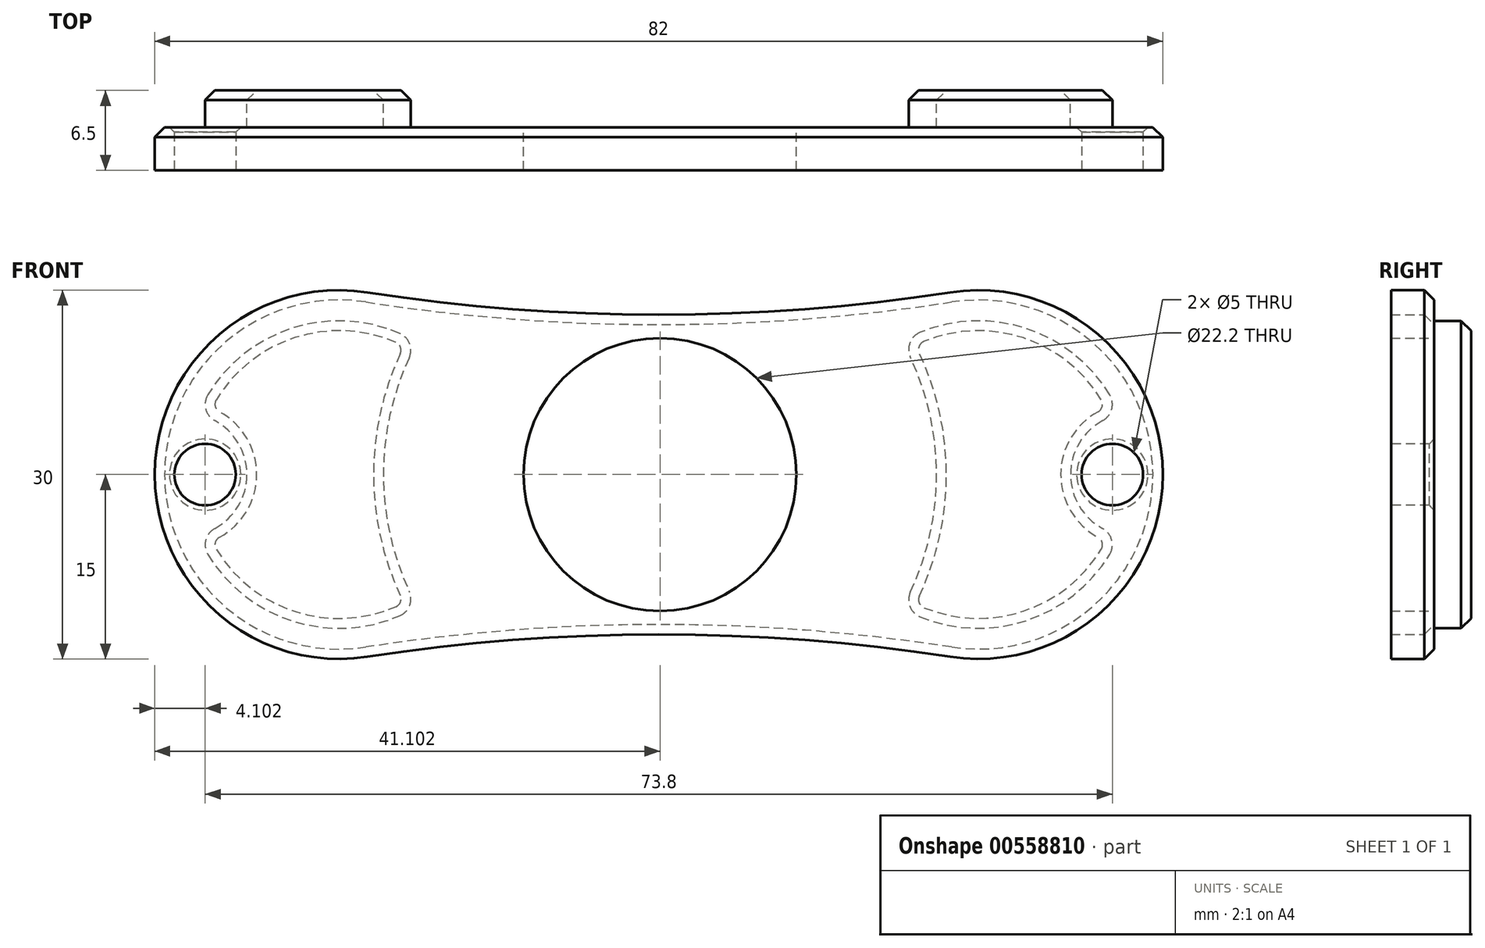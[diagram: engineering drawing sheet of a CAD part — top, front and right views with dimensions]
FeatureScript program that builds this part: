
annotation { "Feature Type Name" : "Feature", "Feature Type Description" : "" }
export const myFeature = defineFeature(function(context is Context, id is Id, definition is map)
    precondition{}
    {
        {
            var Q0;
            Q0=qCreatedBy(makeId("Front.planeOp"),FACE);
            var sketch = newSketch(context, id + "F0", { "sketchPlane" : qUnion([Q0])});
            skCircle(sketch, "E0", {"center": v(-1.84, 0) * mm, "radius": 11.1 * mm});
            skArc(sketch, "E1", {"start": v(-25.64, 14.82) * mm, "mid": v(-42.94, 0) * mm, "end": v(-25.64, -14.82) * mm});
            skArc(sketch, "E2", {"start": v(-25.64, 14.82) * mm, "mid": v(-1.94, 13) * mm, "end": v(21.77, 14.82) * mm});
            skArc(sketch, "E3", {"start": v(21.77, -14.82) * mm, "mid": v(-1.94, -13) * mm, "end": v(-25.64, -14.82) * mm});
            skArc(sketch, "E4.trimOffspring", {"start": v(21.77, -14.82) * mm, "mid": v(39.06, 0) * mm, "end": v(21.77, 14.82) * mm});
            skSolve(sketch);
        }
        {
            var Q0;
            Q0=makeQuery(id+"F0.imprint","IMPRINT",FACE,{"disambiguationData":[TD([[makeQuery(id+"F0.imprint","IMPRINT",EDGE,{"derivedFrom":sQuery(id+"F0.wireOp",EDGE,"E0")}),-1.0]])]});
            extrude(context, id + "F1", {"entities" : qUnion([Q0]), "depth" : 7 * mm, "offsetDistance" : 25 * mm});
        }
        {
            var Q0;
            Q0=makeQuery(id+"F1.opExtrude","CAP_EDGE",EDGE,{"disambiguationData":[OSD([sQuery(id+"F0.wireOp",EDGE,"E1")])],"isStart":false});
            var Q1;
            Q1=makeQuery(id+"F1.opExtrude","CAP_EDGE",EDGE,{"disambiguationData":[OSD([sQuery(id+"F0.wireOp",EDGE,"E3")])],"isStart":false});
            var Q2;
            Q2=makeQuery(id+"F1.opExtrude","CAP_EDGE",EDGE,{"disambiguationData":[OSD([sQuery(id+"F0.wireOp",EDGE,"E3")])],"isStart":true});
            chamfer(context, id + "F2", {"entities" : qUnion([Q0, Q1, Q2]), "width" : .8 * mm, "tangentPropagation" : true});
        }
        {
            var Q0;
            Q0=makeQuery(id+"F1.opExtrude","CAP_FACE",FACE,{"disambiguationData":[OSD([sQuery(id+"F0.wireOp",EDGE,"E0"),sQuery(id+"F0.wireOp",EDGE,"E1"),sQuery(id+"F0.wireOp",EDGE,"E2"),sQuery(id+"F0.wireOp",EDGE,"E3"),sQuery(id+"F0.wireOp",EDGE,"E4.trimOffspring")])],"isStart":false});
            var sketch = newSketch(context, id + "F3", { "sketchPlane" : qUnion([Q0])});
            skCircle(sketch, "E5", {"center": v(-27.94, 0) * mm, "radius": 12.5 * mm});
            skCircle(sketch, "E6", {"center": v(24.06, 0) * mm, "radius": 12.5 * mm});
            skSolve(sketch);
        }
        {
            var Q0;
            Q0=qSketchRegion(id+"F3",true);
            extrude(context, id + "F4", {"entities" : qUnion([Q0]), "operationType" : NewBodyOperationType.ADD, "depth" : 3 * mm, "offsetDistance" : 25 * mm});
        }
        {
            var Q0;
            Q0=makeQuery(id+"F1.opExtrude","CAP_FACE",FACE,{"disambiguationData":[OSD([sQuery(id+"F0.wireOp",EDGE,"E0"),sQuery(id+"F0.wireOp",EDGE,"E1"),sQuery(id+"F0.wireOp",EDGE,"E2"),sQuery(id+"F0.wireOp",EDGE,"E3"),sQuery(id+"F0.wireOp",EDGE,"E4.trimOffspring")])],"isStart":true});
            var sketch = newSketch(context, id + "F5", { "sketchPlane" : qUnion([Q0])});
            skCircle(sketch, "E7", {"center": v(-24.06, 0) * mm, "radius": 12.5 * mm});
            skCircle(sketch, "E8", {"center": v(27.94, 0) * mm, "radius": 12.5 * mm});
            skSolve(sketch);
        }
        {
            var Q0;
            Q0=qSketchRegion(id+"F5",true);
            extrude(context, id + "F6", {"entities" : qUnion([Q0]), "operationType" : NewBodyOperationType.ADD, "depth" : 3 * mm, "offsetDistance" : 25 * mm});
        }
        {
            var Q0;
            Q0=makeQuery(id+"F4.opExtrude","CAP_FACE",FACE,{"disambiguationData":[OSD([sQuery(id+"F3.wireOp",EDGE,"E6")])],"isStart":false});
            var sketch = newSketch(context, id + "F7", { "sketchPlane" : qUnion([Q0])});
            skSolve(sketch);
        }
        {
            var Q0;
            Q0=makeQuery(id+"F4.opExtrude","CAP_FACE",FACE,{"disambiguationData":[OSD([sQuery(id+"F3.wireOp",EDGE,"E5")])],"isStart":false});
            var sketch = newSketch(context, id + "F8", { "sketchPlane" : qUnion([Q0])});
            skCircle(sketch, "E9", {"center": v(-1.84, 0) * mm, "radius": 22.5 * mm});
            skSolve(sketch);
        }
        {
            var Q0;
            Q0=qSketchRegion(id+"F8",true);
            extrude(context, id + "F9", {"entities" : qUnion([Q0]), "operationType" : NewBodyOperationType.REMOVE, "oppositeDirection" : true, "depth" : 3 * mm, "offsetDistance" : 25 * mm});
        }
        {
            var Q0;
            Q0=makeQuery(id+"F6.opExtrude","CAP_FACE",FACE,{"disambiguationData":[OSD([sQuery(id+"F5.wireOp",EDGE,"E7")])],"isStart":false});
            var sketch = newSketch(context, id + "F10", { "sketchPlane" : qUnion([Q0])});
            skCircle(sketch, "E10", {"center": v(1.84, 0) * mm, "radius": 22.5 * mm});
            skSolve(sketch);
        }
        {
            var Q0;
            Q0=qSketchRegion(id+"F10",true);
            extrude(context, id + "F11", {"entities" : qUnion([Q0]), "operationType" : NewBodyOperationType.REMOVE, "oppositeDirection" : true, "depth" : 3 * mm, "offsetDistance" : 25 * mm});
        }
        {
            var Q0;
            Q0=makeQuery(id+"F6.opExtrude","CAP_FACE",FACE,{"disambiguationData":[OSD([sQuery(id+"F5.wireOp",EDGE,"E7")])],"isStart":false});
            var sketch = newSketch(context, id + "F12", { "sketchPlane" : qUnion([Q0])});
            skCircle(sketch, "E11", {"center": v(-36.56, 0) * mm, "radius": 5 * mm});
            skSolve(sketch);
        }
        {
            var Q0;
            Q0=qSketchRegion(id+"F12",true);
            extrude(context, id + "F13", {"entities" : qUnion([Q0]), "operationType" : NewBodyOperationType.REMOVE, "oppositeDirection" : true, "depth" : 3 * mm, "offsetDistance" : 25 * mm});
        }
        {
            var Q0;
            Q0=makeQuery(id+"F6.opExtrude","CAP_FACE",FACE,{"disambiguationData":[OSD([sQuery(id+"F5.wireOp",EDGE,"E8")])],"isStart":false});
            var sketch = newSketch(context, id + "F14", { "sketchPlane" : qUnion([Q0])});
            skCircle(sketch, "E12", {"center": v(40.44, 0) * mm, "radius": 5 * mm});
            skSolve(sketch);
        }
        {
            var Q0;
            Q0=qSketchRegion(id+"F14",true);
            extrude(context, id + "F15", {"entities" : qUnion([Q0]), "operationType" : NewBodyOperationType.REMOVE, "oppositeDirection" : true, "depth" : 3 * mm, "offsetDistance" : 25 * mm});
        }
        {
            var Q0;
            Q0=makeQuery(id+"F4.opExtrude","CAP_FACE",FACE,{"disambiguationData":[OSD([sQuery(id+"F3.wireOp",EDGE,"E5")])],"isStart":false});
            var sketch = newSketch(context, id + "F16", { "sketchPlane" : qUnion([Q0])});
            skCircle(sketch, "E13", {"center": v(-40.44, 0) * mm, "radius": 5 * mm});
            skSolve(sketch);
        }
        {
            var Q0;
            Q0=qSketchRegion(id+"F16",true);
            extrude(context, id + "F17", {"entities" : qUnion([Q0]), "operationType" : NewBodyOperationType.REMOVE, "oppositeDirection" : true, "depth" : 3 * mm, "offsetDistance" : 25 * mm});
        }
        {
            var Q0;
            Q0=makeQuery(id+"F7.imprint","IMPRINT",FACE,{"disambiguationData":[TD([[makeQuery(id+"F7.imprint","IMPRINT",EDGE,{"derivedFrom":makeQuery(id+"F4.opExtrude","CAP_EDGE",EDGE,{"disambiguationData":[OSD([sQuery(id+"F3.wireOp",EDGE,"E6")])],"isStart":false})}),1.0]])]});
            var sketch = newSketch(context, id + "F18", { "sketchPlane" : qUnion([Q0])});
            skCircle(sketch, "E14", {"center": v(36.56, 0) * mm, "radius": 5 * mm});
            skSolve(sketch);
        }
        {
            var Q0;
            Q0=qSketchRegion(id+"F18",true);
            extrude(context, id + "F19", {"entities" : qUnion([Q0]), "operationType" : NewBodyOperationType.REMOVE, "oppositeDirection" : true, "depth" : 3 * mm, "offsetDistance" : 25 * mm});
        }
        {
            var Q0;
            Q0=makeQuery(id+"F17.boolean.opBoolean","INTERSECT",EDGE,{"disambiguationData":[OD(0.0)],"derivedFrom":[makeQuery(id+"F4.opExtrude","SWEPT_FACE",FACE,{"disambiguationData":[OSD([sQuery(id+"F3.wireOp",EDGE,"E5")])]}),makeQuery(id+"F17.opExtrude","SWEPT_FACE",FACE,{"disambiguationData":[OSD([sQuery(id+"F16.wireOp",EDGE,"E13")])]})]});
            var Q1;
            Q1=makeQuery(id+"F17.boolean.opBoolean","INTERSECT",EDGE,{"disambiguationData":[OD(1.0)],"derivedFrom":[makeQuery(id+"F4.opExtrude","SWEPT_FACE",FACE,{"disambiguationData":[OSD([sQuery(id+"F3.wireOp",EDGE,"E5")])]}),makeQuery(id+"F17.opExtrude","SWEPT_FACE",FACE,{"disambiguationData":[OSD([sQuery(id+"F16.wireOp",EDGE,"E13")])]})]});
            var Q2;
            Q2=makeQuery(id+"F9.boolean.opBoolean","INTERSECT",EDGE,{"disambiguationData":[OD(1.0)],"derivedFrom":[makeQuery(id+"F4.opExtrude","SWEPT_FACE",FACE,{"disambiguationData":[OSD([sQuery(id+"F3.wireOp",EDGE,"E5")])]}),makeQuery(id+"F9.opExtrude","SWEPT_FACE",FACE,{"disambiguationData":[OSD([sQuery(id+"F8.wireOp",EDGE,"E9")])]})]});
            var Q3;
            Q3=makeQuery(id+"F9.boolean.opBoolean","INTERSECT",EDGE,{"disambiguationData":[OD(0.0)],"derivedFrom":[makeQuery(id+"F4.opExtrude","SWEPT_FACE",FACE,{"disambiguationData":[OSD([sQuery(id+"F3.wireOp",EDGE,"E5")])]}),makeQuery(id+"F9.opExtrude","SWEPT_FACE",FACE,{"disambiguationData":[OSD([sQuery(id+"F8.wireOp",EDGE,"E9")])]})]});
            var Q4;
            Q4=makeQuery(id+"F9.boolean.opBoolean","INTERSECT",EDGE,{"disambiguationData":[OD(1.0)],"derivedFrom":[makeQuery(id+"F4.opExtrude","SWEPT_FACE",FACE,{"disambiguationData":[OSD([sQuery(id+"F3.wireOp",EDGE,"E6")])]}),makeQuery(id+"F9.opExtrude","SWEPT_FACE",FACE,{"disambiguationData":[OSD([sQuery(id+"F8.wireOp",EDGE,"E9")])]})]});
            var Q5;
            Q5=makeQuery(id+"F9.boolean.opBoolean","INTERSECT",EDGE,{"disambiguationData":[OD(0.0)],"derivedFrom":[makeQuery(id+"F4.opExtrude","SWEPT_FACE",FACE,{"disambiguationData":[OSD([sQuery(id+"F3.wireOp",EDGE,"E6")])]}),makeQuery(id+"F9.opExtrude","SWEPT_FACE",FACE,{"disambiguationData":[OSD([sQuery(id+"F8.wireOp",EDGE,"E9")])]})]});
            var Q6;
            Q6=makeQuery(id+"F19.boolean.opBoolean","INTERSECT",EDGE,{"disambiguationData":[OD(1.0)],"derivedFrom":[makeQuery(id+"F4.opExtrude","SWEPT_FACE",FACE,{"disambiguationData":[OSD([sQuery(id+"F3.wireOp",EDGE,"E6")])]}),makeQuery(id+"F19.opExtrude","SWEPT_FACE",FACE,{"disambiguationData":[OSD([sQuery(id+"F18.wireOp",EDGE,"E14")])]})]});
            var Q7;
            Q7=makeQuery(id+"F19.boolean.opBoolean","INTERSECT",EDGE,{"disambiguationData":[OD(0.0)],"derivedFrom":[makeQuery(id+"F4.opExtrude","SWEPT_FACE",FACE,{"disambiguationData":[OSD([sQuery(id+"F3.wireOp",EDGE,"E6")])]}),makeQuery(id+"F19.opExtrude","SWEPT_FACE",FACE,{"disambiguationData":[OSD([sQuery(id+"F18.wireOp",EDGE,"E14")])]})]});
            var Q8;
            Q8=makeQuery(id+"F11.boolean.opBoolean","INTERSECT",EDGE,{"disambiguationData":[OD(0.0)],"derivedFrom":[makeQuery(id+"F6.opExtrude","SWEPT_FACE",FACE,{"disambiguationData":[OSD([sQuery(id+"F5.wireOp",EDGE,"E8")])]}),makeQuery(id+"F11.opExtrude","SWEPT_FACE",FACE,{"disambiguationData":[OSD([sQuery(id+"F10.wireOp",EDGE,"E10")])]})]});
            var Q9;
            Q9=makeQuery(id+"F11.boolean.opBoolean","INTERSECT",EDGE,{"disambiguationData":[OD(1.0)],"derivedFrom":[makeQuery(id+"F6.opExtrude","SWEPT_FACE",FACE,{"disambiguationData":[OSD([sQuery(id+"F5.wireOp",EDGE,"E8")])]}),makeQuery(id+"F11.opExtrude","SWEPT_FACE",FACE,{"disambiguationData":[OSD([sQuery(id+"F10.wireOp",EDGE,"E10")])]})]});
            var Q10;
            Q10=makeQuery(id+"F15.boolean.opBoolean","INTERSECT",EDGE,{"disambiguationData":[OD(0.0)],"derivedFrom":[makeQuery(id+"F6.opExtrude","SWEPT_FACE",FACE,{"disambiguationData":[OSD([sQuery(id+"F5.wireOp",EDGE,"E8")])]}),makeQuery(id+"F15.opExtrude","SWEPT_FACE",FACE,{"disambiguationData":[OSD([sQuery(id+"F14.wireOp",EDGE,"E12")])]})]});
            var Q11;
            Q11=makeQuery(id+"F15.boolean.opBoolean","INTERSECT",EDGE,{"disambiguationData":[OD(1.0)],"derivedFrom":[makeQuery(id+"F6.opExtrude","SWEPT_FACE",FACE,{"disambiguationData":[OSD([sQuery(id+"F5.wireOp",EDGE,"E8")])]}),makeQuery(id+"F15.opExtrude","SWEPT_FACE",FACE,{"disambiguationData":[OSD([sQuery(id+"F14.wireOp",EDGE,"E12")])]})]});
            var Q12;
            Q12=makeQuery(id+"F11.boolean.opBoolean","INTERSECT",EDGE,{"disambiguationData":[OD(0.0)],"derivedFrom":[makeQuery(id+"F6.opExtrude","SWEPT_FACE",FACE,{"disambiguationData":[OSD([sQuery(id+"F5.wireOp",EDGE,"E7")])]}),makeQuery(id+"F11.opExtrude","SWEPT_FACE",FACE,{"disambiguationData":[OSD([sQuery(id+"F10.wireOp",EDGE,"E10")])]})]});
            var Q13;
            Q13=makeQuery(id+"F11.boolean.opBoolean","INTERSECT",EDGE,{"disambiguationData":[OD(1.0)],"derivedFrom":[makeQuery(id+"F6.opExtrude","SWEPT_FACE",FACE,{"disambiguationData":[OSD([sQuery(id+"F5.wireOp",EDGE,"E7")])]}),makeQuery(id+"F11.opExtrude","SWEPT_FACE",FACE,{"disambiguationData":[OSD([sQuery(id+"F10.wireOp",EDGE,"E10")])]})]});
            var Q14;
            Q14=makeQuery(id+"F13.boolean.opBoolean","INTERSECT",EDGE,{"disambiguationData":[OD(0.0)],"derivedFrom":[makeQuery(id+"F6.opExtrude","SWEPT_FACE",FACE,{"disambiguationData":[OSD([sQuery(id+"F5.wireOp",EDGE,"E7")])]}),makeQuery(id+"F13.opExtrude","SWEPT_FACE",FACE,{"disambiguationData":[OSD([sQuery(id+"F12.wireOp",EDGE,"E11")])]})]});
            var Q15;
            Q15=makeQuery(id+"F13.boolean.opBoolean","INTERSECT",EDGE,{"disambiguationData":[OD(1.0)],"derivedFrom":[makeQuery(id+"F6.opExtrude","SWEPT_FACE",FACE,{"disambiguationData":[OSD([sQuery(id+"F5.wireOp",EDGE,"E7")])]}),makeQuery(id+"F13.opExtrude","SWEPT_FACE",FACE,{"disambiguationData":[OSD([sQuery(id+"F12.wireOp",EDGE,"E11")])]})]});
            fillet(context, id + "F20", {"entities" : qUnion([Q0, Q1, Q2, Q3, Q4, Q5, Q6, Q7, Q8, Q9, Q10, Q11, Q12, Q13, Q14, Q15]), "radius" : 1.5 * mm, "tangentPropagation" : true, "allowEdgeOverflow" : false});
        }
        {
            var Q0;
            Q0=makeQuery(id+"F19.boolean.opBoolean","MERGE",FACE,{"derivedFrom":[makeQuery(id+"F17.boolean.opBoolean","MERGE",FACE,{"derivedFrom":[makeQuery(id+"F9.boolean.opBoolean","MERGE",FACE,{"derivedFrom":[makeQuery(id+"F1.opExtrude","CAP_FACE",FACE,{"disambiguationData":[OSD([sQuery(id+"F0.wireOp",EDGE,"E0"),sQuery(id+"F0.wireOp",EDGE,"E1"),sQuery(id+"F0.wireOp",EDGE,"E2"),sQuery(id+"F0.wireOp",EDGE,"E3"),sQuery(id+"F0.wireOp",EDGE,"E4.trimOffspring")])],"isStart":false}),makeQuery(id+"F9.opExtrude","CAP_FACE",FACE,{"disambiguationData":[OSD([sQuery(id+"F8.wireOp",EDGE,"E9")])],"isStart":false})]}),makeQuery(id+"F17.opExtrude","CAP_FACE",FACE,{"disambiguationData":[OSD([sQuery(id+"F16.wireOp",EDGE,"E13")])],"isStart":false})]}),makeQuery(id+"F19.opExtrude","CAP_FACE",FACE,{"disambiguationData":[OSD([sQuery(id+"F18.wireOp",EDGE,"E14")])],"isStart":false})]});
            var sketch = newSketch(context, id + "F21", { "sketchPlane" : qUnion([Q0])});
            skCircle(sketch, "E15", {"center": v(-38.84, 0) * mm, "radius": 2.5 * mm});
            skSolve(sketch);
        }
        {
            var Q0;
            Q0=qSketchRegion(id+"F21",true);
            extrude(context, id + "F22", {"entities" : qUnion([Q0]), "operationType" : NewBodyOperationType.REMOVE, "oppositeDirection" : true, "depth" : 25 * mm, "offsetDistance" : 25 * mm});
        }
        {
            var Q0;
            Q0=makeQuery(id+"F19.boolean.opBoolean","MERGE",FACE,{"derivedFrom":[makeQuery(id+"F17.boolean.opBoolean","MERGE",FACE,{"derivedFrom":[makeQuery(id+"F9.boolean.opBoolean","MERGE",FACE,{"derivedFrom":[makeQuery(id+"F1.opExtrude","CAP_FACE",FACE,{"disambiguationData":[OSD([sQuery(id+"F0.wireOp",EDGE,"E0"),sQuery(id+"F0.wireOp",EDGE,"E1"),sQuery(id+"F0.wireOp",EDGE,"E2"),sQuery(id+"F0.wireOp",EDGE,"E3"),sQuery(id+"F0.wireOp",EDGE,"E4.trimOffspring")])],"isStart":false}),makeQuery(id+"F9.opExtrude","CAP_FACE",FACE,{"disambiguationData":[OSD([sQuery(id+"F8.wireOp",EDGE,"E9")])],"isStart":false})]}),makeQuery(id+"F17.opExtrude","CAP_FACE",FACE,{"disambiguationData":[OSD([sQuery(id+"F16.wireOp",EDGE,"E13")])],"isStart":false})]}),makeQuery(id+"F19.opExtrude","CAP_FACE",FACE,{"disambiguationData":[OSD([sQuery(id+"F18.wireOp",EDGE,"E14")])],"isStart":false})]});
            var sketch = newSketch(context, id + "F23", { "sketchPlane" : qUnion([Q0])});
            skCircle(sketch, "E16", {"center": v(34.96, 0) * mm, "radius": 2.5 * mm});
            skSolve(sketch);
        }
        {
            var Q0;
            Q0=qSketchRegion(id+"F23",true);
            extrude(context, id + "F24", {"entities" : qUnion([Q0]), "operationType" : NewBodyOperationType.REMOVE, "oppositeDirection" : true, "depth" : 25 * mm, "offsetDistance" : 25 * mm});
        }
        {
            var Q0;
            Q0=makeQuery(id+"F22.boolean.opBoolean","COPY",EDGE,{"derivedFrom":makeQuery(id+"F22.opExtrude","CAP_EDGE",EDGE,{"disambiguationData":[OSD([sQuery(id+"F21.wireOp",EDGE,"E15")])],"isStart":true})});
            var Q1;
            Q1=makeQuery(id+"F24.boolean.opBoolean","COPY",EDGE,{"derivedFrom":makeQuery(id+"F24.opExtrude","CAP_EDGE",EDGE,{"disambiguationData":[OSD([sQuery(id+"F23.wireOp",EDGE,"E16")])],"isStart":true})});
            var Q2;
            Q2=makeQuery(id+"F24.boolean.opBoolean","INTERSECT",EDGE,{"derivedFrom":[makeQuery(id+"F15.boolean.opBoolean","MERGE",FACE,{"derivedFrom":[makeQuery(id+"F13.boolean.opBoolean","MERGE",FACE,{"derivedFrom":[makeQuery(id+"F11.boolean.opBoolean","MERGE",FACE,{"derivedFrom":[makeQuery(id+"F1.opExtrude","CAP_FACE",FACE,{"disambiguationData":[OSD([sQuery(id+"F0.wireOp",EDGE,"E0"),sQuery(id+"F0.wireOp",EDGE,"E1"),sQuery(id+"F0.wireOp",EDGE,"E2"),sQuery(id+"F0.wireOp",EDGE,"E3"),sQuery(id+"F0.wireOp",EDGE,"E4.trimOffspring")])],"isStart":true}),makeQuery(id+"F11.opExtrude","CAP_FACE",FACE,{"disambiguationData":[OSD([sQuery(id+"F10.wireOp",EDGE,"E10")])],"isStart":false})]}),makeQuery(id+"F13.opExtrude","CAP_FACE",FACE,{"disambiguationData":[OSD([sQuery(id+"F12.wireOp",EDGE,"E11")])],"isStart":false})]}),makeQuery(id+"F15.opExtrude","CAP_FACE",FACE,{"disambiguationData":[OSD([sQuery(id+"F14.wireOp",EDGE,"E12")])],"isStart":false})]}),makeQuery(id+"F24.opExtrude","SWEPT_FACE",FACE,{"disambiguationData":[OSD([sQuery(id+"F23.wireOp",EDGE,"E16")])]})]});
            var Q3;
            Q3=makeQuery(id+"F22.boolean.opBoolean","INTERSECT",EDGE,{"derivedFrom":[makeQuery(id+"F15.boolean.opBoolean","MERGE",FACE,{"derivedFrom":[makeQuery(id+"F13.boolean.opBoolean","MERGE",FACE,{"derivedFrom":[makeQuery(id+"F11.boolean.opBoolean","MERGE",FACE,{"derivedFrom":[makeQuery(id+"F1.opExtrude","CAP_FACE",FACE,{"disambiguationData":[OSD([sQuery(id+"F0.wireOp",EDGE,"E0"),sQuery(id+"F0.wireOp",EDGE,"E1"),sQuery(id+"F0.wireOp",EDGE,"E2"),sQuery(id+"F0.wireOp",EDGE,"E3"),sQuery(id+"F0.wireOp",EDGE,"E4.trimOffspring")])],"isStart":true}),makeQuery(id+"F11.opExtrude","CAP_FACE",FACE,{"disambiguationData":[OSD([sQuery(id+"F10.wireOp",EDGE,"E10")])],"isStart":false})]}),makeQuery(id+"F13.opExtrude","CAP_FACE",FACE,{"disambiguationData":[OSD([sQuery(id+"F12.wireOp",EDGE,"E11")])],"isStart":false})]}),makeQuery(id+"F15.opExtrude","CAP_FACE",FACE,{"disambiguationData":[OSD([sQuery(id+"F14.wireOp",EDGE,"E12")])],"isStart":false})]}),makeQuery(id+"F22.opExtrude","SWEPT_FACE",FACE,{"disambiguationData":[OSD([sQuery(id+"F21.wireOp",EDGE,"E15")])]})]});
            chamfer(context, id + "F25", {"entities" : qUnion([Q0, Q1, Q2, Q3]), "width" : 0.4 * mm, "tangentPropagation" : true});
        }
        {
            var Q0;
            Q0=makeQuery(id+"F4.opExtrude","CAP_FACE",FACE,{"disambiguationData":[OSD([sQuery(id+"F3.wireOp",EDGE,"E6")])],"isStart":false});
            var Q1;
            Q1=makeQuery(id+"F4.opExtrude","CAP_FACE",FACE,{"disambiguationData":[OSD([sQuery(id+"F3.wireOp",EDGE,"E5")])],"isStart":false});
            var Q2;
            Q2=makeQuery(id+"F6.opExtrude","CAP_FACE",FACE,{"disambiguationData":[OSD([sQuery(id+"F5.wireOp",EDGE,"E8")])],"isStart":false});
            var Q3;
            Q3=makeQuery(id+"F6.opExtrude","CAP_FACE",FACE,{"disambiguationData":[OSD([sQuery(id+"F5.wireOp",EDGE,"E7")])],"isStart":false});
            chamfer(context, id + "F26", {"entities" : qUnion([Q0, Q1, Q2, Q3]), "width" : .8 * mm, "tangentPropagation" : true});
        }
        {
            var Q0;
            Q0=makeQuery(id+"F4.opExtrude","CAP_FACE",FACE,{"disambiguationData":[OSD([sQuery(id+"F3.wireOp",EDGE,"E5")])],"isStart":false});
            var sketch = newSketch(context, id + "F27", { "sketchPlane" : qUnion([Q0])});
            skLineSegment(sketch, "E17.bottom", {"start": v(-54.9, 24.67) * mm, "end": v(48.36, 24.67) * mm});
            skLineSegment(sketch, "E17.top", {"start": v(-54.9, -24.67) * mm, "end": v(48.36, -24.67) * mm});
            skLineSegment(sketch, "E17.left", {"start": v(-54.9, 24.67) * mm, "end": v(-54.9, -24.67) * mm});
            skLineSegment(sketch, "E17.right", {"start": v(48.36, 24.67) * mm, "end": v(48.36, -24.67) * mm});
            skSolve(sketch);
        }
        {
            var Q0;
            Q0 = qSketchRegion(id + "F27", true);
            extrude(context, id + "F28", {"entities" : qUnion([Q0]), "operationType" : NewBodyOperationType.REMOVE, "oppositeDirection" : true, "depth" : 6.5 * mm, "offsetDistance" : 25 * mm});
        }
    });
